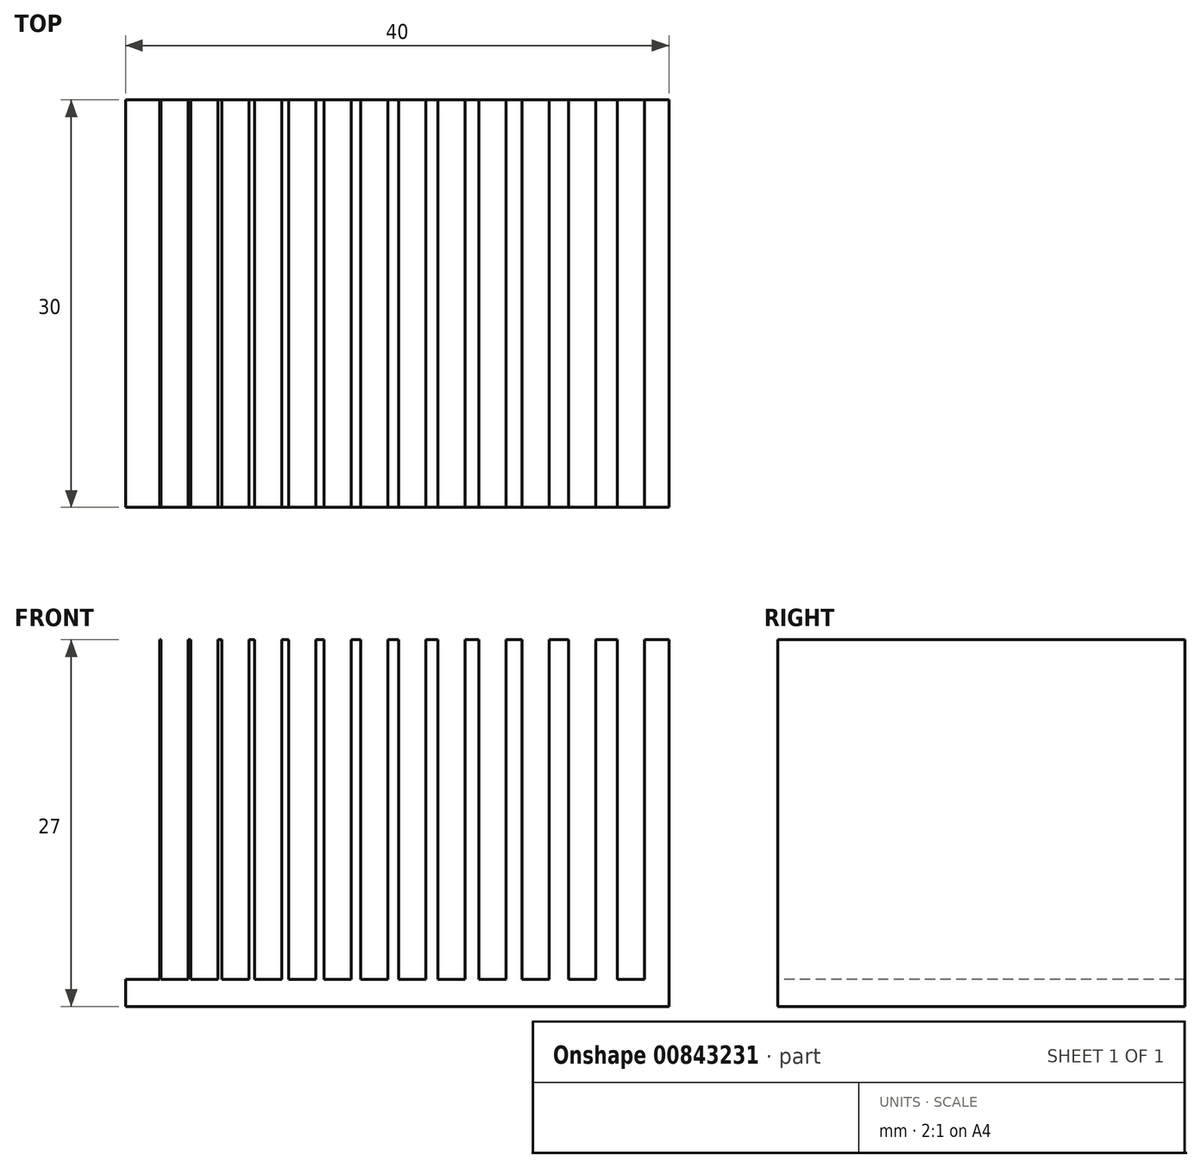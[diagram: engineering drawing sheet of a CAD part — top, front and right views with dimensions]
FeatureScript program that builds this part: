
annotation { "Feature Type Name" : "Feature", "Feature Type Description" : "" }
export const myFeature = defineFeature(function(context is Context, id is Id, definition is map)
    precondition{}
    {
        {
            var Q0;
            Q0=qCreatedBy(makeId("Top.planeOp"),FACE);
            var sketch = newSketch(context, id + "F0", { "sketchPlane" : qUnion([Q0])});
            skLineSegment(sketch, "E0.bottom", {"start": v(-22.07, 16.73) * mm, "end": v(17.93, 16.73) * mm});
            skLineSegment(sketch, "E0.top", {"start": v(-22.07, -13.27) * mm, "end": v(17.93, -13.27) * mm});
            skLineSegment(sketch, "E0.left", {"start": v(-22.07, 16.73) * mm, "end": v(-22.07, -13.27) * mm});
            skLineSegment(sketch, "E0.right", {"start": v(17.93, 16.73) * mm, "end": v(17.93, -13.27) * mm});
            skSolve(sketch);
        }
        {
            var Q0;
            Q0 = qSketchRegion(id + "F0", true);
            extrude(context, id + "F1", {"entities" : qUnion([Q0]), "depth" : 2 * mm, "offsetDistance" : 25 * mm});
        }
        {
            var Q0;
            Q0=makeQuery(id+"F1.opExtrude","CAP_FACE",FACE,{"disambiguationData":[OSD([sQuery(id+"F0.wireOp",EDGE,"E0.bottom"),sQuery(id+"F0.wireOp",EDGE,"E0.top"),sQuery(id+"F0.wireOp",EDGE,"E0.left"),sQuery(id+"F0.wireOp",EDGE,"E0.right")])],"isStart":false});
            var sketch = newSketch(context, id + "F2", { "sketchPlane" : qUnion([Q0])});
            skLineSegment(sketch, "E1.bottom", {"start": v(-17.47, 16.73) * mm, "end": v(-17.27, 16.73) * mm});
            skLineSegment(sketch, "E1.top", {"start": v(-17.47, -13.27) * mm, "end": v(-17.27, -13.27) * mm});
            skLineSegment(sketch, "E1.left", {"start": v(-17.47, 16.73) * mm, "end": v(-17.47, -13.27) * mm});
            skLineSegment(sketch, "E1.right", {"start": v(-17.27, 16.73) * mm, "end": v(-17.27, -13.27) * mm});
            skLineSegment(sketch, "E2.bottom", {"start": v(-15.27, 16.73) * mm, "end": v(-14.97, 16.73) * mm});
            skLineSegment(sketch, "E2.top", {"start": v(-15.27, -13.27) * mm, "end": v(-14.97, -13.27) * mm});
            skLineSegment(sketch, "E2.left", {"start": v(-15.27, 16.73) * mm, "end": v(-15.27, -13.27) * mm});
            skLineSegment(sketch, "E2.right", {"start": v(-14.97, 16.73) * mm, "end": v(-14.97, -13.27) * mm});
            skLineSegment(sketch, "E3.bottom", {"start": v(-12.97, 16.73) * mm, "end": v(-12.57, 16.73) * mm});
            skLineSegment(sketch, "E3.top", {"start": v(-12.97, -13.27) * mm, "end": v(-12.57, -13.27) * mm});
            skLineSegment(sketch, "E3.left", {"start": v(-12.97, 16.73) * mm, "end": v(-12.97, -13.27) * mm});
            skLineSegment(sketch, "E3.right", {"start": v(-12.57, 16.73) * mm, "end": v(-12.57, -13.27) * mm});
            skLineSegment(sketch, "E4.bottom", {"start": v(-10.57, 16.73) * mm, "end": v(-10.07, 16.73) * mm});
            skLineSegment(sketch, "E4.top", {"start": v(-10.57, -13.27) * mm, "end": v(-10.07, -13.27) * mm});
            skLineSegment(sketch, "E4.left", {"start": v(-10.57, 16.73) * mm, "end": v(-10.57, -13.27) * mm});
            skLineSegment(sketch, "E4.right", {"start": v(-10.07, 16.73) * mm, "end": v(-10.07, -13.27) * mm});
            skLineSegment(sketch, "E5.bottom", {"start": v(-8.07, 16.73) * mm, "end": v(-7.47, 16.73) * mm});
            skLineSegment(sketch, "E5.top", {"start": v(-8.07, -13.27) * mm, "end": v(-7.47, -13.27) * mm});
            skLineSegment(sketch, "E5.left", {"start": v(-8.07, 16.73) * mm, "end": v(-8.07, -13.27) * mm});
            skLineSegment(sketch, "E5.right", {"start": v(-7.47, 16.73) * mm, "end": v(-7.47, -13.27) * mm});
            skLineSegment(sketch, "E6.bottom", {"start": v(-5.47, 16.73) * mm, "end": v(-4.77, 16.73) * mm});
            skLineSegment(sketch, "E6.top", {"start": v(-5.47, -13.27) * mm, "end": v(-4.77, -13.27) * mm});
            skLineSegment(sketch, "E6.left", {"start": v(-5.47, 16.73) * mm, "end": v(-5.47, -13.27) * mm});
            skLineSegment(sketch, "E6.right", {"start": v(-4.77, 16.73) * mm, "end": v(-4.77, -13.27) * mm});
            skLineSegment(sketch, "E7.bottom", {"start": v(-2.77, 16.73) * mm, "end": v(-1.97, 16.73) * mm});
            skLineSegment(sketch, "E7.top", {"start": v(-2.77, -13.27) * mm, "end": v(-1.97, -13.27) * mm});
            skLineSegment(sketch, "E7.left", {"start": v(-2.77, 16.73) * mm, "end": v(-2.77, -13.27) * mm});
            skLineSegment(sketch, "E7.right", {"start": v(-1.97, 16.73) * mm, "end": v(-1.97, -13.27) * mm});
            skLineSegment(sketch, "E8.bottom", {"start": v(0.03, 16.73) * mm, "end": v(0.93, 16.73) * mm});
            skLineSegment(sketch, "E8.top", {"start": v(0.03, -13.27) * mm, "end": v(0.93, -13.27) * mm});
            skLineSegment(sketch, "E8.left", {"start": v(0.03, 16.73) * mm, "end": v(0.03, -13.27) * mm});
            skLineSegment(sketch, "E8.right", {"start": v(0.93, 16.73) * mm, "end": v(0.93, -13.27) * mm});
            skLineSegment(sketch, "E9.bottom", {"start": v(2.93, 16.73) * mm, "end": v(3.93, 16.73) * mm});
            skLineSegment(sketch, "E9.top", {"start": v(2.93, -13.27) * mm, "end": v(3.93, -13.27) * mm});
            skLineSegment(sketch, "E9.left", {"start": v(2.93, 16.73) * mm, "end": v(2.93, -13.27) * mm});
            skLineSegment(sketch, "E9.right", {"start": v(3.93, 16.73) * mm, "end": v(3.93, -13.27) * mm});
            skLineSegment(sketch, "E10.bottom", {"start": v(5.93, 16.73) * mm, "end": v(7.13, 16.73) * mm});
            skLineSegment(sketch, "E10.top", {"start": v(5.93, -13.27) * mm, "end": v(7.13, -13.27) * mm});
            skLineSegment(sketch, "E10.left", {"start": v(5.93, 16.73) * mm, "end": v(5.93, -13.27) * mm});
            skLineSegment(sketch, "E10.right", {"start": v(7.13, 16.73) * mm, "end": v(7.13, -13.27) * mm});
            skLineSegment(sketch, "E11.bottom", {"start": v(9.13, 16.73) * mm, "end": v(10.53, 16.73) * mm});
            skLineSegment(sketch, "E11.top", {"start": v(9.13, -13.27) * mm, "end": v(10.53, -13.27) * mm});
            skLineSegment(sketch, "E11.left", {"start": v(9.13, 16.73) * mm, "end": v(9.13, -13.27) * mm});
            skLineSegment(sketch, "E11.right", {"start": v(10.53, 16.73) * mm, "end": v(10.53, -13.27) * mm});
            skLineSegment(sketch, "E12.bottom", {"start": v(12.53, 16.73) * mm, "end": v(14.13, 16.73) * mm});
            skLineSegment(sketch, "E12.top", {"start": v(12.53, -13.27) * mm, "end": v(14.13, -13.27) * mm});
            skLineSegment(sketch, "E12.left", {"start": v(12.53, 16.73) * mm, "end": v(12.53, -13.27) * mm});
            skLineSegment(sketch, "E12.right", {"start": v(14.13, 16.73) * mm, "end": v(14.13, -13.27) * mm});
            skLineSegment(sketch, "E13.bottom", {"start": v(16.13, 16.73) * mm, "end": v(17.93, 16.73) * mm});
            skLineSegment(sketch, "E13.top", {"start": v(16.13, -13.27) * mm, "end": v(17.93, -13.27) * mm});
            skLineSegment(sketch, "E13.left", {"start": v(16.13, 16.73) * mm, "end": v(16.13, -13.27) * mm});
            skLineSegment(sketch, "E13.right", {"start": v(17.93, 16.73) * mm, "end": v(17.93, -13.27) * mm});
            skLineSegment(sketch, "E14.bottom", {"start": v(-19.57, 16.73) * mm, "end": v(-19.47, 16.73) * mm});
            skLineSegment(sketch, "E14.top", {"start": v(-19.57, -13.27) * mm, "end": v(-19.47, -13.27) * mm});
            skLineSegment(sketch, "E14.left", {"start": v(-19.57, 16.73) * mm, "end": v(-19.57, -13.27) * mm});
            skLineSegment(sketch, "E14.right", {"start": v(-19.47, 16.73) * mm, "end": v(-19.47, -13.27) * mm});
            skSolve(sketch);
        }
        {
            var Q0;
            Q0 = qSketchRegion(id + "F2", true);
            extrude(context, id + "F3", {"entities" : qUnion([Q0]), "operationType" : NewBodyOperationType.ADD, "depth" : 25 * mm, "offsetDistance" : 25 * mm});
        }
    });
